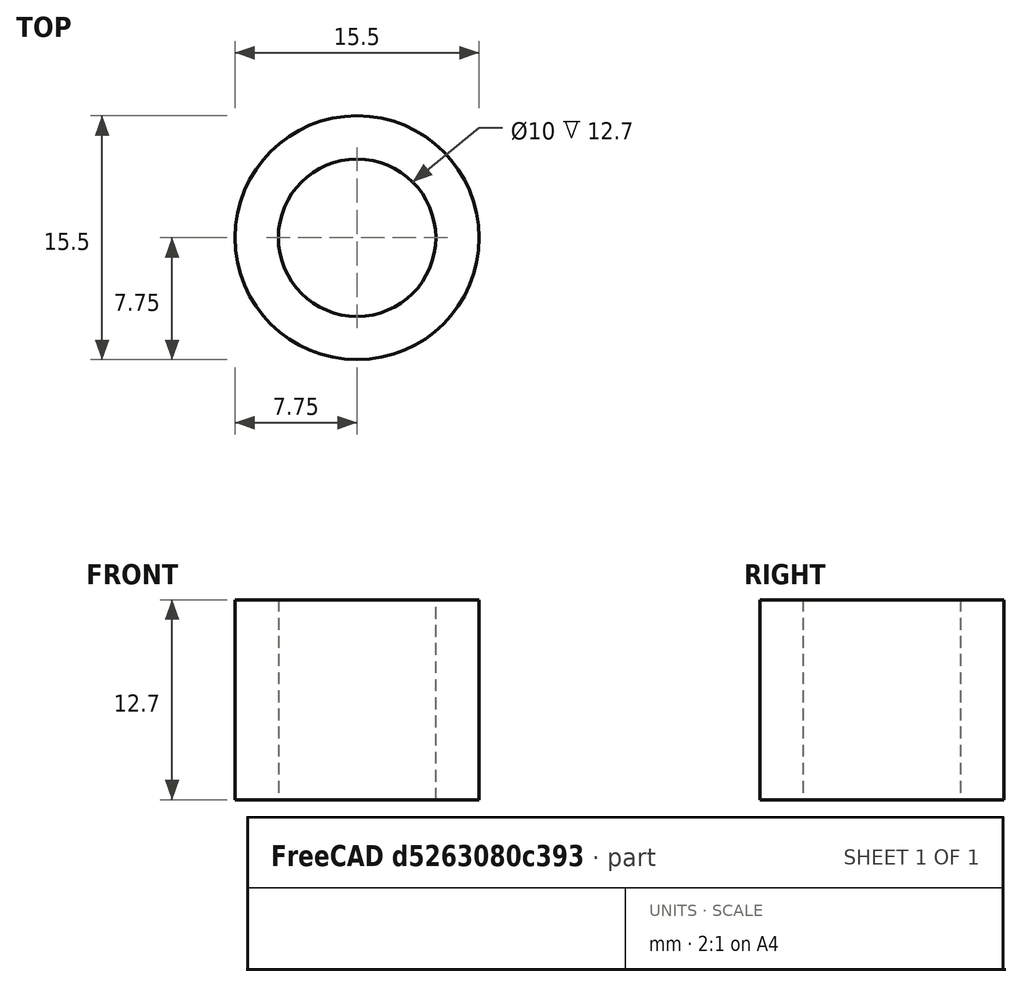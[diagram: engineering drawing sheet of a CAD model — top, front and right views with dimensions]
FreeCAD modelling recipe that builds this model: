
FCSTD DOCUMENT  (FreeCAD 0.20R29177 +426 (Git))
Label: PillowBoltSpacer
License: All rights reserved
LicenseURL: http://en.wikipedia.org/wiki/All_rights_reserved
objects: Sketcher::SketchObject×1, PartDesign::Pad×1, PartDesign::Body×1
note: 4 computed .brp shape members not serialized (recipe doc carries the construction recipe); baked Part::Feature solids carry a one-line shape summary decoded from their .brp

FEATURE [Sketcher::SketchObject] Sketch
  FullyConstrained = true
  MapMode = 5
  Support = -> [XY_Plane]
  sketch-geometry (2):
    g0: Circle CenterX=0 CenterY=0 CenterZ=0 NormalX=0 NormalY=0 NormalZ=1 AngleXU=0 Radius=5
    g1: Circle CenterX=0 CenterY=0 CenterZ=0 NormalX=0 NormalY=0 NormalZ=1 AngleXU=0 Radius=7.75
  constraints (4):
    c: Coincident(g0,g-1)
    c: Coincident(g1,g0)
    c: Diameter(g0) = 10
    c: Diameter(g1) = 15.5
FEATURE [PartDesign::Pad] Pad
  Direction = (0,0,1)
  Length = 12.7
  Length2 = 10
  Profile = -> Sketch
  ReferenceAxis = -> Sketch [N_Axis]
  Type = 0
FEATURE [PartDesign::Body] Body
  Group = -> [Sketch,Pad]
  Origin = -> Origin
  Tip = -> Pad
